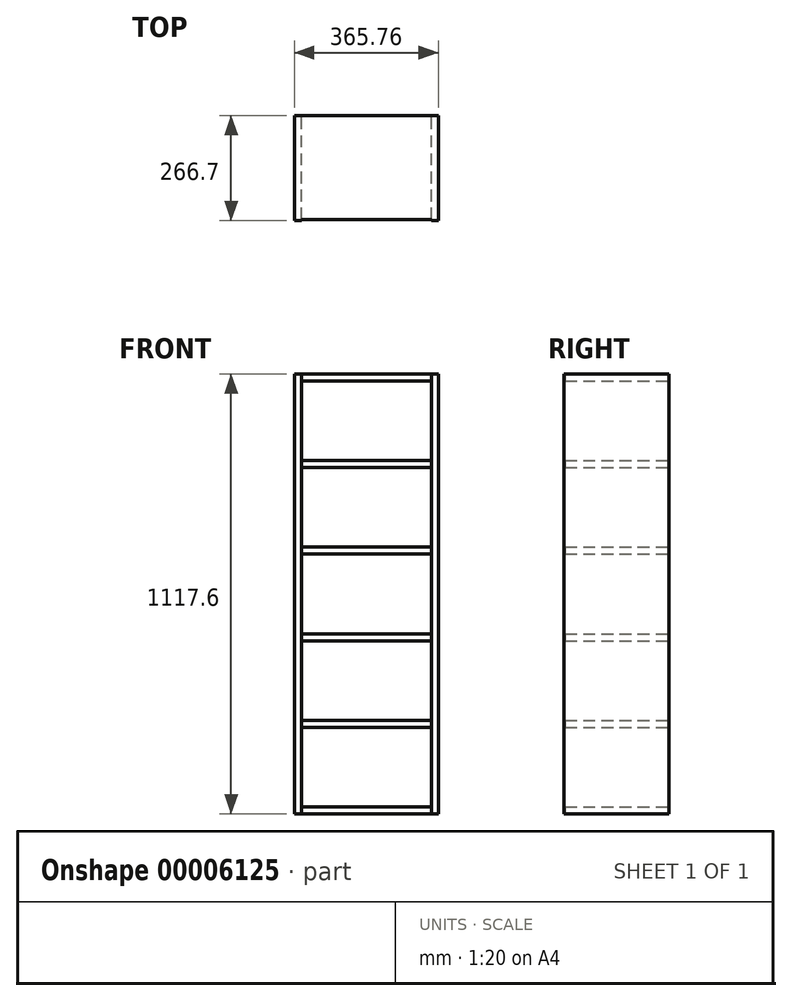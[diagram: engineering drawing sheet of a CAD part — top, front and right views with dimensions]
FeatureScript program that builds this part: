
annotation { "Feature Type Name" : "Feature", "Feature Type Description" : "" }
export const myFeature = defineFeature(function(context is Context, id is Id, definition is map)
    precondition{}
    {
        {
            var Q0;
            Q0=qCreatedBy(makeId("Front.planeOp"),FACE);
            var sketch = newSketch(context, id + "F0", { "sketchPlane" : qUnion([Q0])});
            skLineSegment(sketch, "E0.bottom", {"start": v(0, 1117.6) * mm, "end": v(17.78, 1117.6) * mm});
            skLineSegment(sketch, "E0.top", {"start": v(0, 0) * mm, "end": v(17.78, 0) * mm});
            skLineSegment(sketch, "E0.left", {"start": v(0, 1117.6) * mm, "end": v(0, 0) * mm});
            skLineSegment(sketch, "E0.right", {"start": v(17.78, 1117.6) * mm, "end": v(17.78, 0) * mm});
            skLineSegment(sketch, "E1.bottom", {"start": v(347.98, 1117.6) * mm, "end": v(365.76, 1117.6) * mm});
            skLineSegment(sketch, "E1.top", {"start": v(347.98, 0) * mm, "end": v(365.76, 0) * mm});
            skLineSegment(sketch, "E1.left", {"start": v(347.98, 1117.6) * mm, "end": v(347.98, 0) * mm});
            skLineSegment(sketch, "E1.right", {"start": v(365.76, 1117.6) * mm, "end": v(365.76, 0) * mm});
            skLineSegment(sketch, "E2.bottom", {"start": v(17.78, 17.78) * mm, "end": v(347.98, 17.78) * mm});
            skLineSegment(sketch, "E2.top", {"start": v(17.78, 0) * mm, "end": v(347.98, 0) * mm});
            skLineSegment(sketch, "E2.left", {"start": v(17.78, 17.78) * mm, "end": v(17.78, 0) * mm});
            skLineSegment(sketch, "E2.right", {"start": v(347.98, 17.78) * mm, "end": v(347.98, 0) * mm});
            skLineSegment(sketch, "E3.0.1.0", {"start": v(347.98, 219.96) * mm, "end": v(365.76, 219.96) * mm});
            skLineSegment(sketch, "E3.0.1.1", {"start": v(0, 219.96) * mm, "end": v(17.78, 219.96) * mm});
            skLineSegment(sketch, "E3.0.1.2", {"start": v(17.78, 237.74) * mm, "end": v(347.98, 237.74) * mm});
            skLineSegment(sketch, "E3.0.1.3", {"start": v(17.78, 237.74) * mm, "end": v(17.78, 219.96) * mm});
            skLineSegment(sketch, "E3.0.1.4", {"start": v(17.78, 219.96) * mm, "end": v(347.98, 219.96) * mm});
            skLineSegment(sketch, "E3.0.1.5", {"start": v(347.98, 237.74) * mm, "end": v(347.98, 219.96) * mm});
            skLineSegment(sketch, "E3.0.2.0", {"start": v(347.98, 439.93) * mm, "end": v(365.76, 439.93) * mm});
            skLineSegment(sketch, "E3.0.2.1", {"start": v(0, 439.93) * mm, "end": v(17.78, 439.93) * mm});
            skLineSegment(sketch, "E3.0.2.2", {"start": v(17.78, 457.7) * mm, "end": v(347.98, 457.7) * mm});
            skLineSegment(sketch, "E3.0.2.3", {"start": v(17.78, 457.7) * mm, "end": v(17.78, 439.93) * mm});
            skLineSegment(sketch, "E3.0.2.4", {"start": v(17.78, 439.93) * mm, "end": v(347.98, 439.93) * mm});
            skLineSegment(sketch, "E3.0.2.5", {"start": v(347.98, 457.7) * mm, "end": v(347.98, 439.93) * mm});
            skLineSegment(sketch, "E3.0.3.0", {"start": v(347.98, 659.9) * mm, "end": v(365.76, 659.9) * mm});
            skLineSegment(sketch, "E3.0.3.1", {"start": v(0, 659.9) * mm, "end": v(17.78, 659.9) * mm});
            skLineSegment(sketch, "E3.0.3.2", {"start": v(17.78, 677.67) * mm, "end": v(347.98, 677.67) * mm});
            skLineSegment(sketch, "E3.0.3.3", {"start": v(17.78, 677.67) * mm, "end": v(17.78, 659.9) * mm});
            skLineSegment(sketch, "E3.0.3.4", {"start": v(17.78, 659.9) * mm, "end": v(347.98, 659.9) * mm});
            skLineSegment(sketch, "E3.0.3.5", {"start": v(347.98, 677.67) * mm, "end": v(347.98, 659.9) * mm});
            skLineSegment(sketch, "E3.0.4.0", {"start": v(347.98, 879.86) * mm, "end": v(365.76, 879.86) * mm});
            skLineSegment(sketch, "E3.0.4.1", {"start": v(0, 879.86) * mm, "end": v(17.78, 879.86) * mm});
            skLineSegment(sketch, "E3.0.4.2", {"start": v(17.78, 897.64) * mm, "end": v(347.98, 897.64) * mm});
            skLineSegment(sketch, "E3.0.4.3", {"start": v(17.78, 897.64) * mm, "end": v(17.78, 879.86) * mm});
            skLineSegment(sketch, "E3.0.4.4", {"start": v(17.78, 879.86) * mm, "end": v(347.98, 879.86) * mm});
            skLineSegment(sketch, "E3.0.4.5", {"start": v(347.98, 897.64) * mm, "end": v(347.98, 879.86) * mm});
            skLineSegment(sketch, "E3.0.5.0", {"start": v(347.98, 1099.82) * mm, "end": v(365.76, 1099.82) * mm});
            skLineSegment(sketch, "E3.0.5.1", {"start": v(0, 1099.82) * mm, "end": v(17.78, 1099.82) * mm});
            skLineSegment(sketch, "E3.0.5.2", {"start": v(17.78, 1117.6) * mm, "end": v(347.98, 1117.6) * mm});
            skLineSegment(sketch, "E3.0.5.3", {"start": v(17.78, 1117.6) * mm, "end": v(17.78, 1099.82) * mm});
            skLineSegment(sketch, "E3.0.5.4", {"start": v(17.78, 1099.82) * mm, "end": v(347.98, 1099.82) * mm});
            skLineSegment(sketch, "E3.0.5.5", {"start": v(347.98, 1117.6) * mm, "end": v(347.98, 1099.82) * mm});
            skLineSegment(sketch, "E3.direction1", {"start": v(347.98, 0) * mm, "end": v(347.98, 0) * mm});
            skLineSegment(sketch, "E3.direction2", {"start": v(347.98, 0) * mm, "end": v(347.98, 219.96) * mm, "construction": true});
            skSolve(sketch);
        }
        {
            var Q0;
            {var subQ4=sQuery(id+"F0.wireOp",EDGE,"E0.top");Q0=makeQuery(id+"F0.imprint","IMPRINT",FACE,{"disambiguationData":[TD([[makeQuery(id+"F0.imprint","IMPRINT",EDGE,{"derivedFrom":subQ4}),1.0]])]});}
            var Q1;
            {var subQ2=sQuery(id+"F0.wireOp",EDGE,"E3.0.1.1");Q1=makeQuery(id+"F0.imprint","IMPRINT",FACE,{"disambiguationData":[TD([[makeQuery(id+"F0.imprint","IMPRINT",EDGE,{"derivedFrom":subQ2}),1.0]])]});}
            var Q2;
            {var subQ1=sQuery(id+"F0.wireOp",EDGE,"E3.0.2.1");Q2=makeQuery(id+"F0.imprint","IMPRINT",FACE,{"disambiguationData":[TD([[makeQuery(id+"F0.imprint","IMPRINT",EDGE,{"derivedFrom":subQ1}),1.0]])]});}
            var Q3;
            {var subQ2=sQuery(id+"F0.wireOp",EDGE,"E3.0.3.1");Q3=makeQuery(id+"F0.imprint","IMPRINT",FACE,{"disambiguationData":[TD([[makeQuery(id+"F0.imprint","IMPRINT",EDGE,{"derivedFrom":subQ2}),1.0]])]});}
            var Q4;
            {var subQ2=sQuery(id+"F0.wireOp",EDGE,"E3.0.4.1");Q4=makeQuery(id+"F0.imprint","IMPRINT",FACE,{"disambiguationData":[TD([[makeQuery(id+"F0.imprint","IMPRINT",EDGE,{"derivedFrom":subQ2}),1.0]])]});}
            var Q5;
            {var subQ2=sQuery(id+"F0.wireOp",EDGE,"E0.bottom");Q5=makeQuery(id+"F0.imprint","IMPRINT",FACE,{"disambiguationData":[TD([[makeQuery(id+"F0.imprint","IMPRINT",EDGE,{"derivedFrom":subQ2}),-1.0]])]});}
            var Q6;
            {var subQ2=sQuery(id+"F0.wireOp",EDGE,"E3.0.4.0");Q6=makeQuery(id+"F0.imprint","IMPRINT",FACE,{"disambiguationData":[TD([[makeQuery(id+"F0.imprint","IMPRINT",EDGE,{"derivedFrom":subQ2}),1.0]])]});}
            var Q7;
            {var subQ2=sQuery(id+"F0.wireOp",EDGE,"E3.0.3.0");Q7=makeQuery(id+"F0.imprint","IMPRINT",FACE,{"disambiguationData":[TD([[makeQuery(id+"F0.imprint","IMPRINT",EDGE,{"derivedFrom":subQ2}),1.0]])]});}
            var Q8;
            {var subQ2=sQuery(id+"F0.wireOp",EDGE,"E3.0.2.0");Q8=makeQuery(id+"F0.imprint","IMPRINT",FACE,{"disambiguationData":[TD([[makeQuery(id+"F0.imprint","IMPRINT",EDGE,{"derivedFrom":subQ2}),1.0]])]});}
            var Q9;
            {var subQ2=sQuery(id+"F0.wireOp",EDGE,"E3.0.1.0");Q9=makeQuery(id+"F0.imprint","IMPRINT",FACE,{"disambiguationData":[TD([[makeQuery(id+"F0.imprint","IMPRINT",EDGE,{"derivedFrom":subQ2}),1.0]])]});}
            var Q10;
            {var subQ3=sQuery(id+"F0.wireOp",EDGE,"E1.top");Q10=makeQuery(id+"F0.imprint","IMPRINT",FACE,{"disambiguationData":[TD([[makeQuery(id+"F0.imprint","IMPRINT",EDGE,{"derivedFrom":subQ3}),1.0]])]});}
            var Q11;
            {var subQ2=sQuery(id+"F0.wireOp",EDGE,"E1.bottom");Q11=makeQuery(id+"F0.imprint","IMPRINT",FACE,{"disambiguationData":[TD([[makeQuery(id+"F0.imprint","IMPRINT",EDGE,{"derivedFrom":subQ2}),-1.0]])]});}
            extrude(context, id + "F1", {"entities" : qUnion([Q0, Q1, Q2, Q3, Q4, Q5, Q6, Q7, Q8, Q9, Q10, Q11]), "depth" : 266.7 * mm});
        }
        {
            var Q0;
            Q0=makeQuery(id+"F0.imprint","IMPRINT",FACE,{"disambiguationData":[TD([[makeQuery(id+"F0.imprint","IMPRINT",EDGE,{"derivedFrom":sQuery(id+"F0.wireOp",EDGE,"E3.0.5.2")}),-1.0]])]});
            var Q1;
            Q1=makeQuery(id+"F0.imprint","IMPRINT",FACE,{"disambiguationData":[TD([[makeQuery(id+"F0.imprint","IMPRINT",EDGE,{"derivedFrom":sQuery(id+"F0.wireOp",EDGE,"E3.0.4.2")}),-1.0]])]});
            var Q2;
            Q2=makeQuery(id+"F0.imprint","IMPRINT",FACE,{"disambiguationData":[TD([[makeQuery(id+"F0.imprint","IMPRINT",EDGE,{"derivedFrom":sQuery(id+"F0.wireOp",EDGE,"E3.0.3.2")}),-1.0]])]});
            var Q3;
            Q3=makeQuery(id+"F0.imprint","IMPRINT",FACE,{"disambiguationData":[TD([[makeQuery(id+"F0.imprint","IMPRINT",EDGE,{"derivedFrom":sQuery(id+"F0.wireOp",EDGE,"E3.0.2.2")}),-1.0]])]});
            var Q4;
            Q4=makeQuery(id+"F0.imprint","IMPRINT",FACE,{"disambiguationData":[TD([[makeQuery(id+"F0.imprint","IMPRINT",EDGE,{"derivedFrom":sQuery(id+"F0.wireOp",EDGE,"E3.0.1.2")}),-1.0]])]});
            var Q5;
            Q5=makeQuery(id+"F0.imprint","IMPRINT",FACE,{"disambiguationData":[TD([[makeQuery(id+"F0.imprint","IMPRINT",EDGE,{"derivedFrom":sQuery(id+"F0.wireOp",EDGE,"E2.bottom")}),-1.0]])]});
            extrude(context, id + "F2", {"entities" : qUnion([Q0, Q1, Q2, Q3, Q4, Q5]), "operationType" : NewBodyOperationType.ADD, "depth" : 264.16 * mm});
        }
    });
